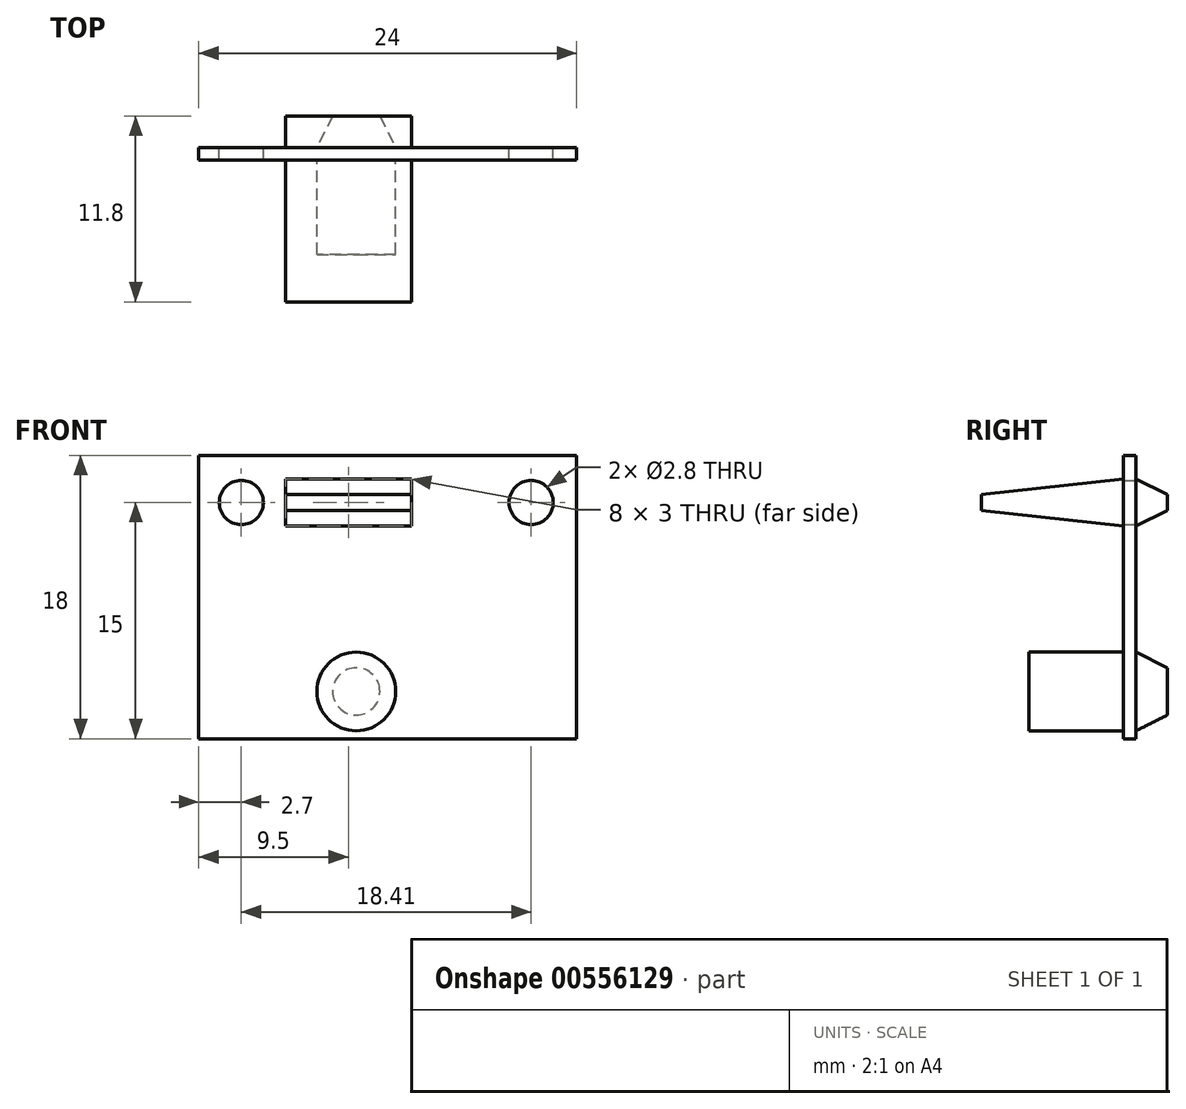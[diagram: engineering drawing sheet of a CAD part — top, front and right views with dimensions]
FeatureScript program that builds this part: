
annotation { "Feature Type Name" : "Feature", "Feature Type Description" : "" }
export const myFeature = defineFeature(function(context is Context, id is Id, definition is map)
    precondition{}
    {
        {
            var Q0;
            Q0=qCreatedBy(makeId("Front.planeOp"),FACE);
            var sketch = newSketch(context, id + "F0", { "sketchPlane" : qUnion([Q0])});
            skLineSegment(sketch, "E0.bottom", {"start": v(12, 9) * mm, "end": v(-12, 9) * mm});
            skLineSegment(sketch, "E0.top", {"start": v(12, -9) * mm, "end": v(-12, -9) * mm});
            skLineSegment(sketch, "E0.left", {"start": v(12, 9) * mm, "end": v(12, -9) * mm});
            skLineSegment(sketch, "E0.right", {"start": v(-12, 9) * mm, "end": v(-12, -9) * mm});
            skPoint(sketch, "E0.middle", {"position": v(0, 0) * mm});
            skLineSegment(sketch, "E1", {"start": v(-12, 6) * mm, "end": v(12, 6) * mm, "construction": true});
            skPoint(sketch, "E2", {"position": v(-9.3, 6) * mm});
            skPoint(sketch, "E3", {"position": v(9.1, 6) * mm});
            skLineSegment(sketch, "E4.bottom", {"start": v(1.5, 7.5) * mm, "end": v(-6.5, 7.5) * mm});
            skLineSegment(sketch, "E4.top", {"start": v(1.5, 4.5) * mm, "end": v(-6.5, 4.5) * mm});
            skLineSegment(sketch, "E4.left", {"start": v(1.5, 7.5) * mm, "end": v(1.5, 4.5) * mm});
            skLineSegment(sketch, "E4.right", {"start": v(-6.5, 7.5) * mm, "end": v(-6.5, 4.5) * mm});
            skPoint(sketch, "E4.middle", {"position": v(-2.5, 6) * mm});
            skCircle(sketch, "E5", {"center": v(-2, -6) * mm, "radius": 2.5 * mm});
            skSolve(sketch);
        }
        {
            var Q0;
            Q0=makeQuery(id+"F0.imprint","IMPRINT",FACE,{"disambiguationData":[TD([[makeQuery(id+"F0.imprint","IMPRINT",EDGE,{"derivedFrom":sQuery(id+"F0.wireOp",EDGE,"E0.bottom")}),1.0]])]});
            var Q1;
            Q1=makeQuery(id+"F0.imprint","IMPRINT",FACE,{"disambiguationData":[TD([[makeQuery(id+"F0.imprint","IMPRINT",EDGE,{"derivedFrom":sQuery(id+"F0.wireOp",EDGE,"E4.bottom")}),1.0]])]});
            var Q2;
            Q2=makeQuery(id+"F0.imprint","IMPRINT",FACE,{"disambiguationData":[TD([[makeQuery(id+"F0.imprint","IMPRINT",EDGE,{"derivedFrom":sQuery(id+"F0.wireOp",EDGE,"E5")}),1.0]])]});
            extrude(context, id + "F1", {"entities" : qUnion([Q0, Q1, Q2]), "depth" : 0.8 * mm, "offsetDistance" : 25 * mm});
        }
        {
            var Q0;
            Q0=sQuery(id+"F0.wireOp",VERTEX,"E2");
            var Q1;
            Q1=sQuery(id+"F0.wireOp",VERTEX,"E3");
            var Q2;
            Q2=makeQuery(id+"F1.opExtrude","SWEPT_BODY",BODY,{"disambiguationData":[OSD([sQuery(id+"F0.wireOp",EDGE,"E0.bottom"),sQuery(id+"F0.wireOp",EDGE,"E0.top"),sQuery(id+"F0.wireOp",EDGE,"E0.left"),sQuery(id+"F0.wireOp",EDGE,"E0.right")])]});
            hole(context, id + "F2", {"style" : HoleStyle.SIMPLE, "endStyle" : HoleEndStyle.THROUGH, "oppositeDirection" : true, "holeDiameter" : 2.8 * mm, "majorDiameter" : 5 * mm, "isTappedThrough" : true, "tappedDepth" : 12 * mm, "tapClearance" : 3, "locations" : qUnion([Q0, Q1]), "scope" : qUnion([Q2])});
        }
        {
            var Q0;
            Q0=makeQuery(id+"F0.imprint","IMPRINT",FACE,{"disambiguationData":[TD([[makeQuery(id+"F0.imprint","IMPRINT",EDGE,{"derivedFrom":sQuery(id+"F0.wireOp",EDGE,"E4.bottom")}),1.0]])]});
            var Q1;
            Q1=makeQuery(id+"F0.imprint","IMPRINT",FACE,{"disambiguationData":[TD([[makeQuery(id+"F0.imprint","IMPRINT",EDGE,{"derivedFrom":sQuery(id+"F0.wireOp",EDGE,"E5")}),1.0]])]});
            extrude(context, id + "F3", {"entities" : qUnion([Q0, Q1]), "operationType" : NewBodyOperationType.ADD, "oppositeDirection" : true, "depth" : 2 * mm, "offsetDistance" : 25 * mm});
        }
        {
            var Q0;
            Q0=makeQuery(id+"F3.opExtrude","CAP_EDGE",EDGE,{"disambiguationData":[OSD([sQuery(id+"F0.wireOp",EDGE,"E4.top")])],"isStart":false});
            var Q1;
            Q1=makeQuery(id+"F3.opExtrude","CAP_EDGE",EDGE,{"disambiguationData":[OSD([sQuery(id+"F0.wireOp",EDGE,"E4.bottom")])],"isStart":false});
            chamfer(context, id + "F4", {"entities" : qUnion([Q0, Q1]), "chamferType" : ChamferType.TWO_OFFSETS, "width1" : 1 * mm, "oppositeDirection" : false, "width2" : 2 * mm, "tangentPropagation" : true});
        }
        {
            var Q0;
            Q0=makeQuery(id+"F3.opExtrude","CAP_EDGE",EDGE,{"disambiguationData":[OSD([sQuery(id+"F0.wireOp",EDGE,"E5")])],"isStart":false});
            chamfer(context, id + "F5", {"entities" : qUnion([Q0]), "chamferType" : ChamferType.TWO_OFFSETS, "width1" : 2 * mm, "oppositeDirection" : false, "width2" : 1 * mm, "tangentPropagation" : true});
        }
        {
            var Q0;
            Q0=makeQuery(id+"F0.imprint","IMPRINT",FACE,{"disambiguationData":[TD([[makeQuery(id+"F0.imprint","IMPRINT",EDGE,{"derivedFrom":sQuery(id+"F0.wireOp",EDGE,"E5")}),1.0]])]});
            extrude(context, id + "F6", {"entities" : qUnion([Q0]), "operationType" : NewBodyOperationType.ADD, "depth" : (6 + 0.8) * mm, "offsetDistance" : 25 * mm});
        }
        {
            var Q0;
            Q0=makeQuery(id+"F0.imprint","IMPRINT",FACE,{"disambiguationData":[TD([[makeQuery(id+"F0.imprint","IMPRINT",EDGE,{"derivedFrom":sQuery(id+"F0.wireOp",EDGE,"E4.bottom")}),1.0]])]});
            extrude(context, id + "F7", {"entities" : qUnion([Q0]), "operationType" : NewBodyOperationType.ADD, "depth" : (9 + 0.8) * mm, "offsetDistance" : 25 * mm});
        }
        {
            var Q0;
            Q0=makeQuery(id+"F7.opExtrude","CAP_EDGE",EDGE,{"disambiguationData":[OSD([sQuery(id+"F0.wireOp",EDGE,"E4.bottom")])],"isStart":false});
            var Q1;
            Q1=makeQuery(id+"F7.opExtrude","CAP_EDGE",EDGE,{"disambiguationData":[OSD([sQuery(id+"F0.wireOp",EDGE,"E4.top")])],"isStart":false});
            chamfer(context, id + "F8", {"entities" : qUnion([Q0, Q1]), "chamferType" : ChamferType.TWO_OFFSETS, "width1" : 1 * mm, "oppositeDirection" : false, "width2" : 9 * mm, "tangentPropagation" : true});
        }
    });
